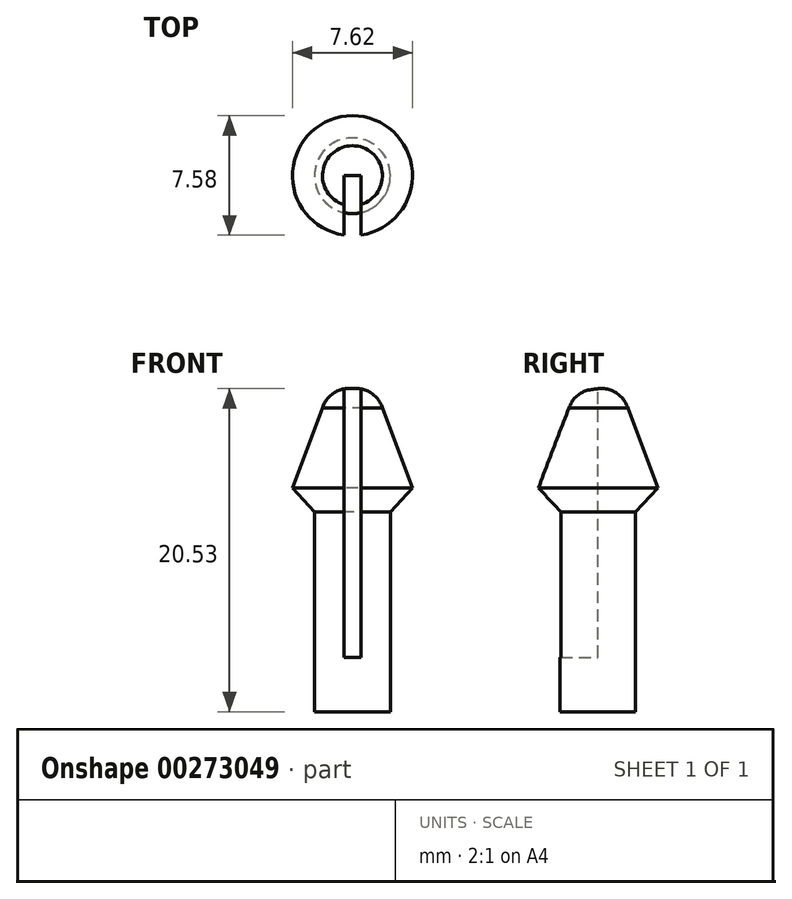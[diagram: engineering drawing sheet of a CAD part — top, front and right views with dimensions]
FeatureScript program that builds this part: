
annotation { "Feature Type Name" : "Feature", "Feature Type Description" : "" }
export const myFeature = defineFeature(function(context is Context, id is Id, definition is map)
    precondition{}
    {
        {
            var Q0;
            Q0=qCreatedBy(makeId("Top.planeOp"),FACE);
            var sketch = newSketch(context, id + "F0", { "sketchPlane" : qUnion([Q0])});
            skCircle(sketch, "E0", {"center": v(0, 0) * mm, "radius": 2.4 * mm});
            skSolve(sketch);
        }
        {
            var Q0;
            Q0=qCreatedBy(makeId("Top.planeOp"),FACE);
            cPlane(context, id + "F1", {"entities" : qUnion([Q0]), "cplaneType" : CPlaneType.OFFSET, "offset" : 1.52 * mm, "width" : 152.4 * mm, "height" : 152.4 * mm});
        }
        {
            var Q0;
            Q0=qCreatedBy(id+"F1.planeOp",FACE);
            var sketch = newSketch(context, id + "F2", { "sketchPlane" : qUnion([Q0])});
            skCircle(sketch, "E1", {"center": v(0, 0) * mm, "radius": 3.81 * mm});
            skSolve(sketch);
        }
        {
            var Q0;
            Q0=qCreatedBy(id+"F1.planeOp",FACE);
            cPlane(context, id + "F3", {"entities" : qUnion([Q0]), "cplaneType" : CPlaneType.OFFSET, "offset" : 5.08 * mm, "width" : 152.4 * mm, "height" : 152.4 * mm});
        }
        {
            var Q0;
            Q0=qCreatedBy(id+"F3.planeOp",FACE);
            var sketch = newSketch(context, id + "F4", { "sketchPlane" : qUnion([Q0])});
            skCircle(sketch, "E2", {"center": v(0, 0) * mm, "radius": 1.9 * mm});
            skSolve(sketch);
        }
        {
            var Q0;
            Q0=makeQuery(id+"F4.imprint","IMPRINT",FACE,{"disambiguationData":[TD([[makeQuery(id+"F4.imprint","IMPRINT",EDGE,{"derivedFrom":sQuery(id+"F4.wireOp",EDGE,"E2")}),1.0]])]});
            var Q1;
            Q1=makeQuery(id+"F2.imprint","IMPRINT",FACE,{"disambiguationData":[TD([[makeQuery(id+"F2.imprint","IMPRINT",EDGE,{"derivedFrom":sQuery(id+"F2.wireOp",EDGE,"E1")}),1.0]])]});
            loft(context, id + "F5", {"sheetProfilesArray" : [{ "sheetProfileEntities" : qUnion([Q0]) }, { "sheetProfileEntities" : qUnion([Q1]) }]});
        }
        {
            var Q1;
            Q1=makeQuery(id+"F5.opLoft","CAP_FACE",FACE,{"disambiguationData":[OSD([makeQuery(id+"F2.imprint","IMPRINT",FACE,{"disambiguationData":[TD([[makeQuery(id+"F2.imprint","IMPRINT",EDGE,{"derivedFrom":sQuery(id+"F2.wireOp",EDGE,"E1")}),1.0]])]})])],"isStart":true});
            var Q2;
            Q2=makeQuery(id+"F0.imprint","IMPRINT",FACE,{"disambiguationData":[TD([[makeQuery(id+"F0.imprint","IMPRINT",EDGE,{"derivedFrom":sQuery(id+"F0.wireOp",EDGE,"E0")}),1.0]])]});
            loft(context, id + "F6", {"operationType" : NewBodyOperationType.ADD, "sheetProfilesArray" : [{ "sheetProfileEntities" : qUnion([Q1]) }, { "sheetProfileEntities" : qUnion([Q2]) }]});
        }
        {
            var Q0;
            Q0=makeQuery(id+"F0.imprint","IMPRINT",FACE,{"disambiguationData":[TD([[makeQuery(id+"F0.imprint","IMPRINT",EDGE,{"derivedFrom":sQuery(id+"F0.wireOp",EDGE,"E0")}),1.0]])]});
            extrude(context, id + "F7", {"entities" : qUnion([Q0]), "operationType" : NewBodyOperationType.ADD, "oppositeDirection" : true, "depth" : 12.7 * mm});
        }
        {
            var Q0;
            Q0=qCreatedBy(makeId("Front.planeOp"),FACE);
            var sketch = newSketch(context, id + "F8", { "sketchPlane" : qUnion([Q0])});
            skLineSegment(sketch, "E3", {"start": v(0, 0) * mm, "end": v(0, 6.6) * mm});
            skLineSegment(sketch, "E4", {"start": v(0, 6.6) * mm, "end": v(-1.9, 6.6) * mm});
            skLineSegment(sketch, "E5", {"start": v(-1.9, 6.6) * mm, "end": v(0, 7.82) * mm});
            skSolve(sketch);
        }
        {
            var Q0;
            Q0=qCreatedBy(makeId("Front.planeOp"),FACE);
            var sketch = newSketch(context, id + "F9", { "sketchPlane" : qUnion([Q0])});
            skArc(sketch, "E6", {"start": v(0, 7.82) * mm, "mid": v(-1.17, 7.56) * mm, "end": v(-1.9, 6.6) * mm});
            skLineSegment(sketch, "E7", {"start": v(-1.9, 6.6) * mm, "end": v(0, 6.6) * mm});
            skLineSegment(sketch, "E8", {"start": v(0, 6.6) * mm, "end": v(0, 7.82) * mm});
            skSolve(sketch);
        }
        {
            var Q0;
            Q0=qCreatedBy(makeId("Front.planeOp"),FACE);
            var sketch = newSketch(context, id + "F10", { "sketchPlane" : qUnion([Q0])});
            skLineSegment(sketch, "E9", {"start": v(0, 7.82) * mm, "end": v(0, 6.6) * mm});
            skLineSegment(sketch, "E10", {"start": v(0, 6.6) * mm, "end": v(-1.9, 6.6) * mm});
            skSolve(sketch);
        }
        {
            var Q0;
            Q0=makeQuery(id+"F9.imprint","IMPRINT",FACE,{"disambiguationData":[TD([[makeQuery(id+"F9.imprint","IMPRINT",EDGE,{"derivedFrom":sQuery(id+"F9.wireOp",EDGE,"E6")}),1.0]])]});
            var Q1;
            Q1=sQuery(id+"F10.wireOp",EDGE,"E9");
            revolve(context, id + "F11", {"operationType" : NewBodyOperationType.ADD, "entities" : qUnion([Q0]), "axis" : qUnion([Q1]), "revolveType" : RevolveType.FULL});
        }
        {
            var Q0;
            Q0=qCreatedBy(makeId("Front.planeOp"),FACE);
            var sketch = newSketch(context, id + "F12", { "sketchPlane" : qUnion([Q0])});
            skLineSegment(sketch, "E11.bottom", {"start": v(0.55, -9.25) * mm, "end": v(-0.55, -9.25) * mm});
            skLineSegment(sketch, "E11.top", {"start": v(0.55, 29.56) * mm, "end": v(-0.55, 29.56) * mm});
            skLineSegment(sketch, "E11.left", {"start": v(0.55, -9.25) * mm, "end": v(0.55, 29.56) * mm});
            skLineSegment(sketch, "E11.right", {"start": v(-0.55, -9.25) * mm, "end": v(-0.55, 29.56) * mm});
            skPoint(sketch, "E11.middle", {"position": v(0, 10.16) * mm});
            skSolve(sketch);
        }
        {
            var Q0;
            Q0=makeQuery(id+"F12.imprint","IMPRINT",FACE,{"disambiguationData":[TD([[makeQuery(id+"F12.imprint","IMPRINT",EDGE,{"derivedFrom":sQuery(id+"F12.wireOp",EDGE,"E11.bottom")}),-1.0]])]});
            extrude(context, id + "F13", {"entities" : qUnion([Q0]), "operationType" : NewBodyOperationType.REMOVE, "depth" : 25.4 * mm});
        }
    });
